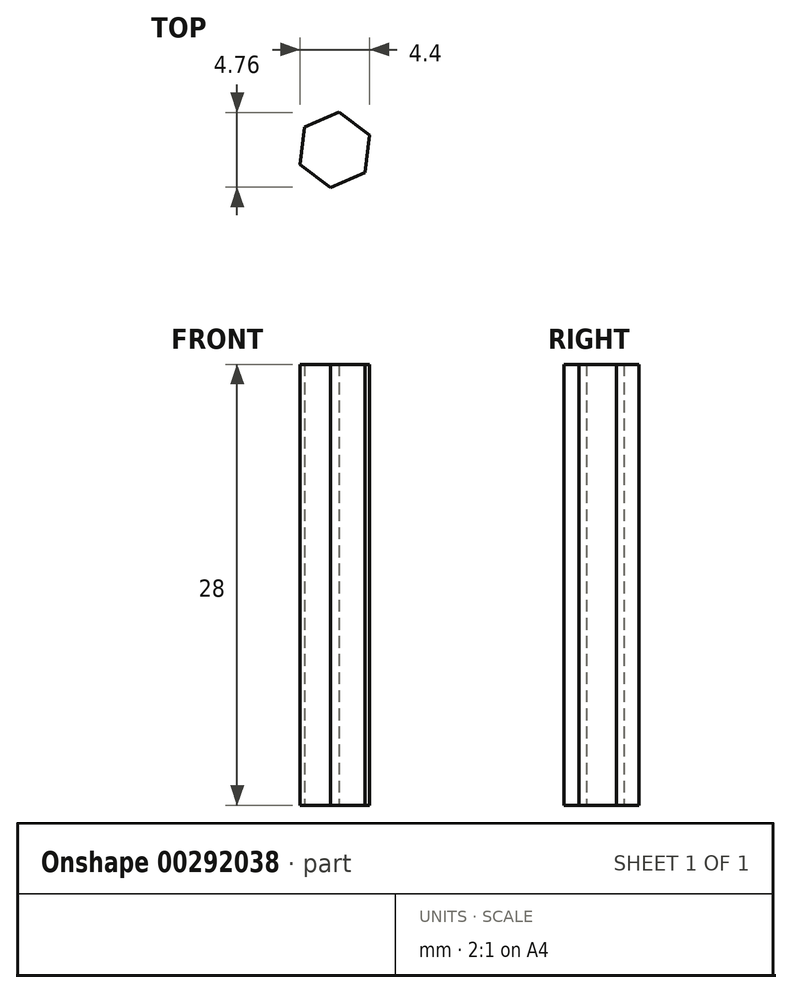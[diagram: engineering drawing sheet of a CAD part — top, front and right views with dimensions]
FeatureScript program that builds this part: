
annotation { "Feature Type Name" : "Feature", "Feature Type Description" : "" }
export const myFeature = defineFeature(function(context is Context, id is Id, definition is map)
    precondition{}
    {
        {
            var Q0;
            Q0=qCreatedBy(makeId("Top.planeOp"),FACE);
            var sketch = newSketch(context, id + "F0", { "sketchPlane" : qUnion([Q0])});
            skCircle(sketch, "E0.cCircle", {"center": v(0, 0) * mm, "radius": 2.08 * mm, "construction": true});
            skLineSegment(sketch, "E0.0", {"start": v(0.28, 2.38) * mm, "end": v(2.2, 0.95) * mm});
            skLineSegment(sketch, "E0.1", {"start": v(2.2, 0.95) * mm, "end": v(1.93, -1.43) * mm});
            skLineSegment(sketch, "E0.2", {"start": v(1.93, -1.43) * mm, "end": v(-0.28, -2.38) * mm});
            skLineSegment(sketch, "E0.3", {"start": v(-0.28, -2.38) * mm, "end": v(-2.2, -0.95) * mm});
            skLineSegment(sketch, "E0.4", {"start": v(-2.2, -0.95) * mm, "end": v(-1.93, 1.43) * mm});
            skLineSegment(sketch, "E0.5", {"start": v(-1.93, 1.43) * mm, "end": v(0.28, 2.38) * mm});
            skPoint(sketch, "E0.0.midPoint", {"position": v(1.24, 1.67) * mm});
            skSolve(sketch);
        }
        {
            var Q0;
            Q0=makeQuery(id+"F0.imprint","IMPRINT",FACE,{"disambiguationData":[TD([[makeQuery(id+"F0.imprint","IMPRINT",EDGE,{"derivedFrom":sQuery(id+"F0.wireOp",EDGE,"E0.0")}),-1.0]])]});
            extrude(context, id + "F1", {"entities" : qUnion([Q0]), "depth" : 28 * mm});
        }
    });
